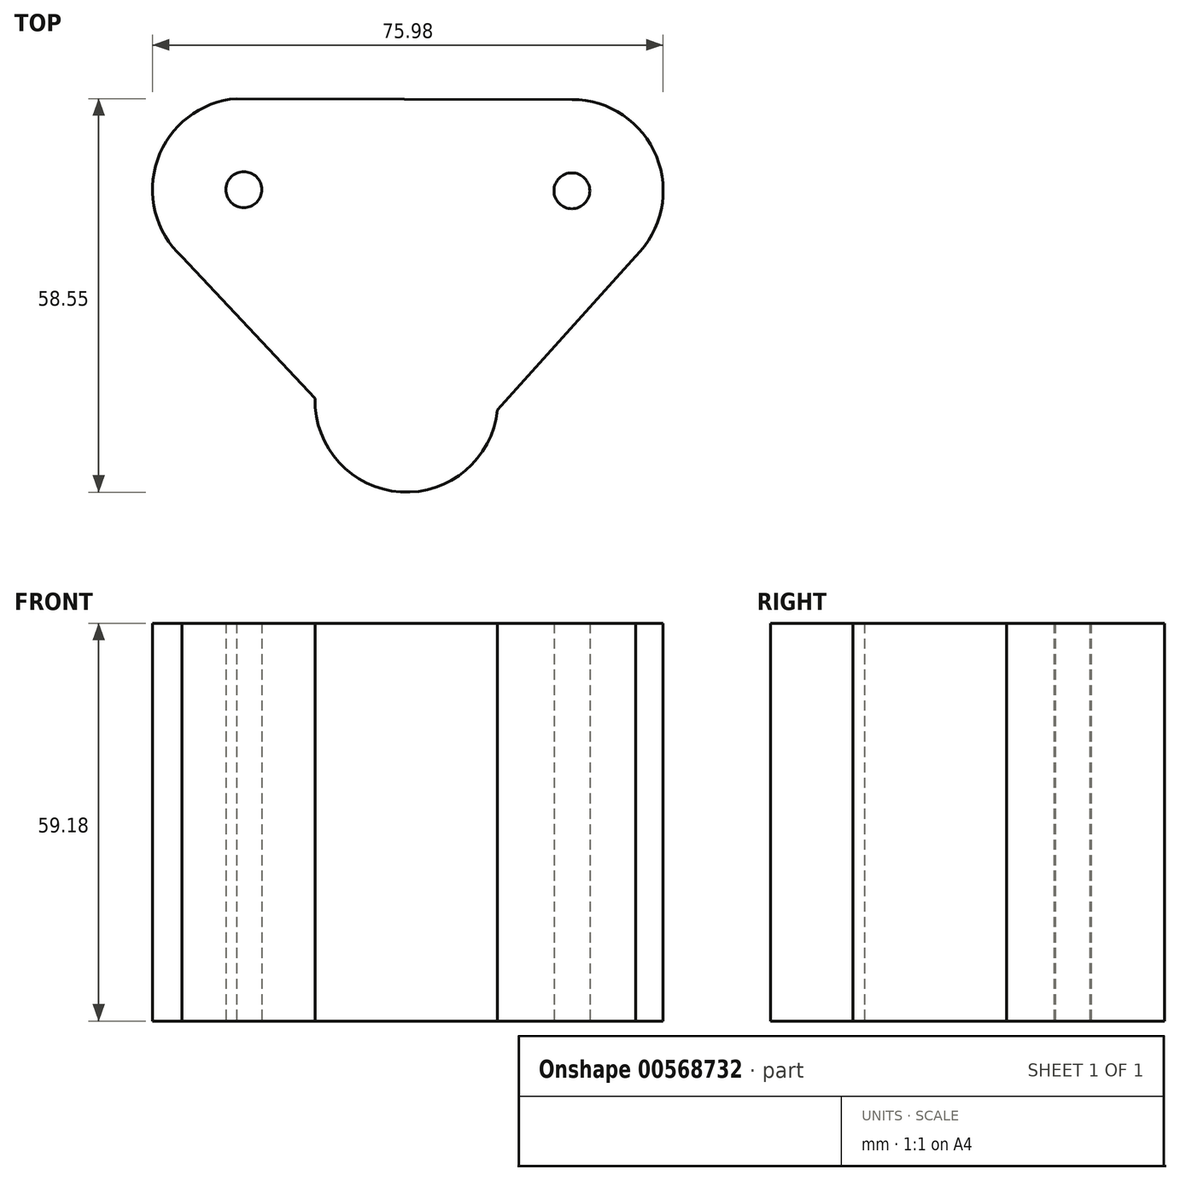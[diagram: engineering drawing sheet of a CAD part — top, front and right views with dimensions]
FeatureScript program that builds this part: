
annotation { "Feature Type Name" : "Feature", "Feature Type Description" : "" }
export const myFeature = defineFeature(function(context is Context, id is Id, definition is map)
    precondition{}
    {
        {
            var Q0;
            Q0=qCreatedBy(makeId("Top.planeOp"),FACE);
            var sketch = newSketch(context, id + "F0", { "sketchPlane" : qUnion([Q0])});
            skCircle(sketch, "E0", {"center": v(-24.2, 0.17) * mm, "radius": 2.67 * mm});
            skCircle(sketch, "E1", {"center": v(24.61, 0) * mm, "radius": 2.67 * mm});
            skLineSegment(sketch, "E2", {"start": v(34.07, -9.75) * mm, "end": v(13.52, -32.59) * mm});
            skLineSegment(sketch, "E3", {"start": v(-25.27, 13.72) * mm, "end": v(24.65, 13.59) * mm});
            skLineSegment(sketch, "E4", {"start": v(-34.72, -8.42) * mm, "end": v(-13.58, -30.86) * mm});
            skArc(sketch, "E5", {"start": v(-25.27, 13.72) * mm, "mid": v(-37.04, 4.6) * mm, "end": v(-33.4, -9.82) * mm});
            skArc(sketch, "E6", {"start": v(34.07, -9.75) * mm, "mid": v(37.21, 5.09) * mm, "end": v(24.65, 13.59) * mm});
            skArc(sketch, "E7", {"start": v(-13.58, -30.86) * mm, "mid": v(-0.87, -44.8) * mm, "end": v(13.52, -32.59) * mm});
            skSolve(sketch);
        }
        {
            var Q0;
            {var subQ0=sQuery(id+"F0.wireOp",EDGE,"E2");Q0=makeQuery(id+"F0.imprint","IMPRINT",FACE,{"disambiguationData":[TD([[makeQuery(id+"F0.imprint","IMPRINT",EDGE,{"derivedFrom":subQ0}),-1.0]])]});}
            extrude(context, id + "F1", {"entities" : qUnion([Q0]), "depth" : 59.18 * mm, "offsetDistance" : 25.4 * mm});
        }
        {
            var Q0;
            Q0 = qSketchRegion(id + "F0", true);
            extrude(context, id + "F2", {"entities" : qUnion([Q0]), "operationType" : NewBodyOperationType.ADD, "depth" : 59.18 * mm, "offsetDistance" : 25.4 * mm});
        }
    });
